# Revit family: Dozownik_mydla_w_plynie 1 l DUO
name_source: partatom
category: Furniture
units: mm (PartAtom-declared; Revit-internal decimal feet)

## family parameters
Always vertical = Yes
Cut with Voids When Loaded = No
Host = Wall
Room Calculation Point = No
Shared = No

## types (1)
- S1000SPP
    Depth / Glebokosc = 72 mm  [stored 0.23622 ft]
    Description = Dozownik mydła w płynie 1 l DUO to naścienny stalowy dystrybutor o wykończeniu polerowanym. Jest bardzo prosty w montażu, użytkowaniu oraz konserwacji. Jego uniwersalny design sprawia, że można go bez problemu wkomponować w przestrzeń każdej toalety użytku publicznego. Najlepiej sprawdzi się w miejscach o średnim i dużym natężeniu ruchu, jak np. galerie handlowe czy restauracje. Jest on wyposażony w ergonomiczny przycisk dozowania mydła oraz w okienko do kontrolowania jego poziomu. Podajnik do mydła DUO jest gwarancją wysokiej jakości i dużej trwałości.
    Height / Wysokosc = 202 mm  [stored 0.66273 ft]
    Manufacturer = FANECO.com
    Manufacturer code / Kod producenta = 5901764295815
    Material = Stal nierdzewna AISI 304 polerowana
    Material finish / Wykonczenie = Stal nierdzewna 304 polerowana, połysk
    Model = DUO
    Product code / Kod produktu = S1000SPP
    Type Comments = https://Dozownik mydła w płynie 1 l DUO
    URL = https://faneco.com
    Weight / Waga = 0.6 kg
    Width / Szerokosc = 122 mm  [stored 0.400262 ft]

note: [stored X ft] marks values corroborated as IEEE doubles in the binary element streams (Revit-internal decimal feet)

## geometry (parser evidence)
native form markers: Sweep x7
no freeform markers — native parametric forms only
